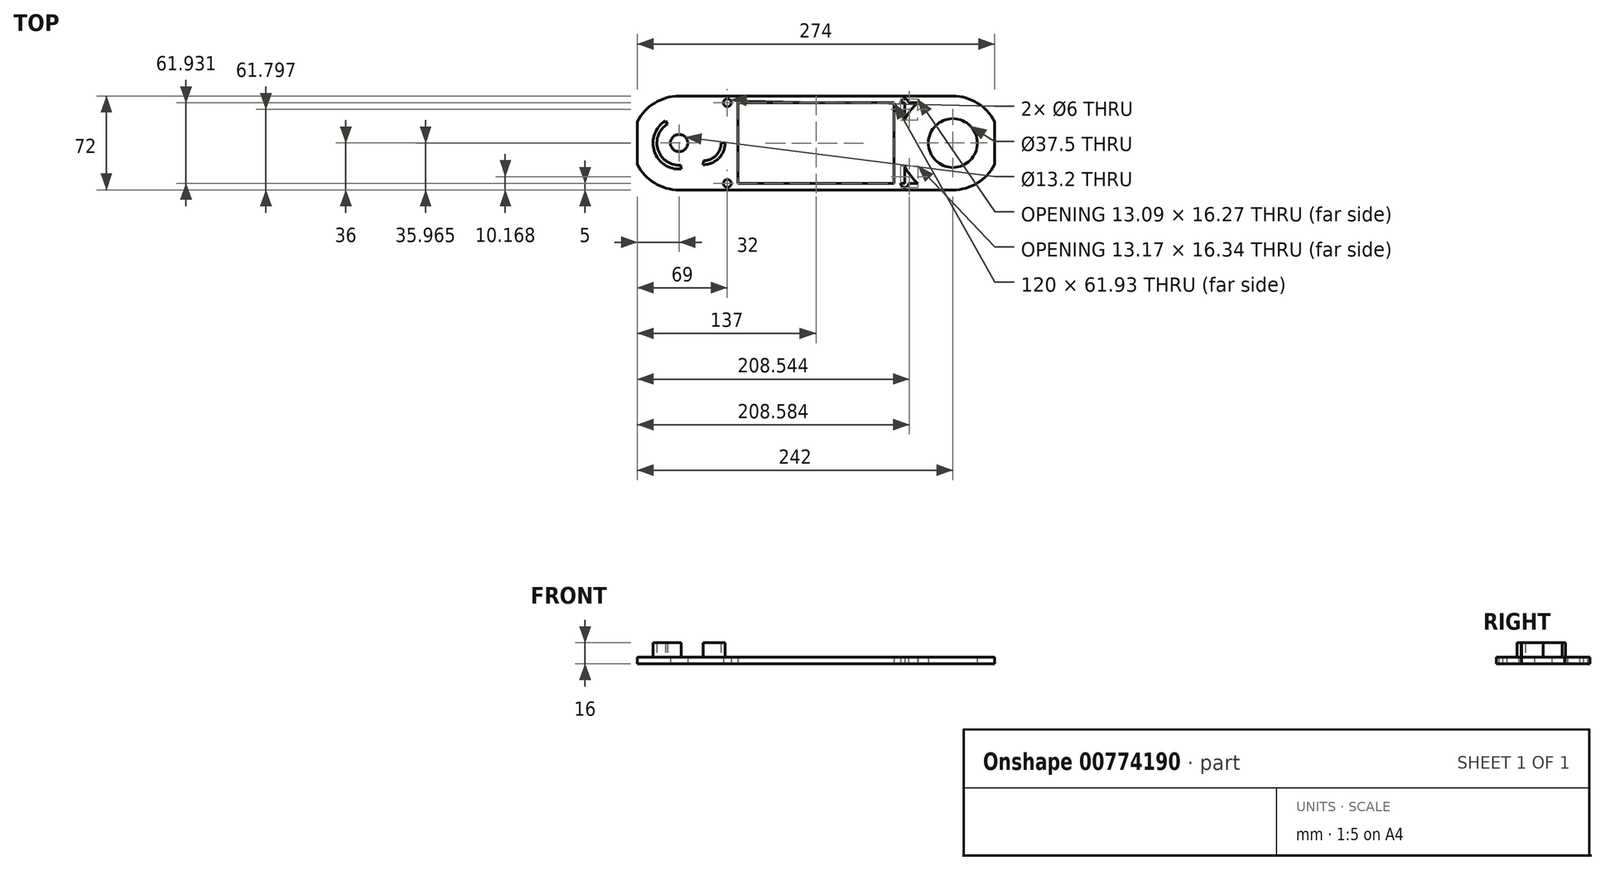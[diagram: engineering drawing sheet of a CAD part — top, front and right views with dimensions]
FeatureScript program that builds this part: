
annotation { "Feature Type Name" : "Feature", "Feature Type Description" : "" }
export const myFeature = defineFeature(function(context is Context, id is Id, definition is map)
    precondition{}
    {
        {
            var Q0;
            Q0=qCreatedBy(makeId("Top.planeOp"),FACE);
            var sketch = newSketch(context, id + "F0", { "sketchPlane" : qUnion([Q0])});
            skCircle(sketch, "E0", {"center": v(0, 0) * mm, "radius": 36 * mm});
            skCircle(sketch, "E1", {"center": v(210, 0) * mm, "radius": 36 * mm});
            skLineSegment(sketch, "E2", {"start": v(0, 36) * mm, "end": v(210, 36) * mm});
            skLineSegment(sketch, "E3", {"start": v(210, -36) * mm, "end": v(0, -36) * mm});
            skCircle(sketch, "E4", {"center": v(0, 0) * mm, "radius": 6.6 * mm});
            skCircle(sketch, "E5", {"center": v(0, 0) * mm, "radius": 10 * mm});
            skCircle(sketch, "E6", {"center": v(0, 0) * mm, "radius": 30 * mm});
            skCircle(sketch, "E7", {"center": v(210, 0) * mm, "radius": 30 * mm});
            skCircle(sketch, "E8", {"center": v(210, 0) * mm, "radius": 18.75 * mm});
            skCircle(sketch, "E9", {"center": v(210, 0) * mm, "radius": 21.5 * mm});
            skLineSegment(sketch, "E10", {"start": v(18.42, 30.93) * mm, "end": v(191.58, 30.93) * mm});
            skLineSegment(sketch, "E11", {"start": v(18.3, -31) * mm, "end": v(191.7, -31) * mm});
            skLineSegment(sketch, "E12", {"start": v(165, 30.93) * mm, "end": v(165, -31) * mm});
            skLineSegment(sketch, "E13", {"start": v(45, 30.93) * mm, "end": v(45, -31) * mm});
            skCircle(sketch, "E14", {"center": v(210, 0) * mm, "radius": 41 * mm});
            skCircle(sketch, "E15", {"center": v(0, 0) * mm, "radius": 41 * mm});
            skLineSegment(sketch, "E16.bottom", {"start": v(37, 30.93) * mm, "end": v(173, 30.93) * mm});
            skLineSegment(sketch, "E16.top", {"start": v(37, -31) * mm, "end": v(173, -31) * mm});
            skLineSegment(sketch, "E16.left", {"start": v(37, 30.93) * mm, "end": v(37, -31) * mm});
            skLineSegment(sketch, "E16.right", {"start": v(173, 30.93) * mm, "end": v(173, -31) * mm});
            skCircle(sketch, "E17", {"center": v(37, 30.93) * mm, "radius": 3 * mm});
            skCircle(sketch, "E18", {"center": v(37, -31) * mm, "radius": 3 * mm});
            skCircle(sketch, "E19", {"center": v(173, 30.93) * mm, "radius": 3 * mm});
            skCircle(sketch, "E20", {"center": v(173, -31) * mm, "radius": 3 * mm});
            skLineSegment(sketch, "E21", {"start": v(-32, -16.5) * mm, "end": v(-32, 16.5) * mm});
            skLineSegment(sketch, "E22", {"start": v(242, -16.5) * mm, "end": v(242, 16.5) * mm});
            skSolve(sketch);
        }
        {
            var Q0;
            {var subQ0=sQuery(id+"F0.wireOp",EDGE,"E16.left");var subQ1=sQuery(id+"F0.wireOp",EDGE,"E15");var subQ2=makeQuery(id+"F0.imprint","INTERSECT",VERTEX,{"disambiguationData":[OD(0.0)],"derivedFrom":[subQ1,subQ0]});Q0=makeQuery(id+"F0.imprint","IMPRINT",FACE,{"disambiguationData":[TD([[makeQuery(id+"F0.imprint","IMPRINT",EDGE,{"disambiguationData":[TD([[subQ2,1.0]])],"derivedFrom":subQ1}),1.0]])]});}
            var Q1;
            Q1=makeQuery(id+"F0.imprint","IMPRINT",FACE,{"disambiguationData":[TD([[makeQuery(id+"F0.imprint","IMPRINT",EDGE,{"derivedFrom":sQuery(id+"F0.wireOp",EDGE,"E4")}),-1.0]])]});
            var Q2;
            {var subQ0=sQuery(id+"F0.wireOp",EDGE,"E2");var subQ1=sQuery(id+"F0.wireOp",EDGE,"E1");var subQ2=makeQuery(id+"F0.imprint","INTERSECT",VERTEX,{"derivedFrom":[subQ1,subQ0]});Q2=makeQuery(id+"F0.imprint","IMPRINT",FACE,{"disambiguationData":[TD([[makeQuery(id+"F0.imprint","IMPRINT",EDGE,{"disambiguationData":[TD([[subQ2,-1.0]])],"derivedFrom":subQ1}),-1.0]])]});}
            var Q3;
            Q3=makeQuery(id+"F0.imprint","IMPRINT",FACE,{"disambiguationData":[TD([[makeQuery(id+"F0.imprint","IMPRINT",EDGE,{"derivedFrom":sQuery(id+"F0.wireOp",EDGE,"E5")}),-1.0]])]});
            var Q4;
            Q4=makeQuery(id+"F0.imprint","IMPRINT",FACE,{"disambiguationData":[TD([[makeQuery(id+"F0.imprint","IMPRINT",EDGE,{"derivedFrom":sQuery(id+"F0.wireOp",EDGE,"E8")}),-1.0]])]});
            var Q5;
            {var subQ0=sQuery(id+"F0.wireOp",EDGE,"E3");var subQ1=sQuery(id+"F0.wireOp",EDGE,"E0");var subQ2=makeQuery(id+"F0.imprint","INTERSECT",VERTEX,{"derivedFrom":[subQ1,subQ0]});Q5=makeQuery(id+"F0.imprint","IMPRINT",FACE,{"disambiguationData":[TD([[makeQuery(id+"F0.imprint","IMPRINT",EDGE,{"disambiguationData":[TD([[subQ2,-1.0]])],"derivedFrom":subQ1}),-1.0]])]});}
            var Q6;
            Q6=makeQuery(id+"F0.imprint","IMPRINT",FACE,{"disambiguationData":[TD([[makeQuery(id+"F0.imprint","IMPRINT",EDGE,{"derivedFrom":sQuery(id+"F0.wireOp",EDGE,"E7")}),-1.0]])]});
            var Q7;
            Q7=makeQuery(id+"F0.imprint","IMPRINT",FACE,{"disambiguationData":[TD([[makeQuery(id+"F0.imprint","IMPRINT",EDGE,{"derivedFrom":sQuery(id+"F0.wireOp",EDGE,"E7")}),1.0]])]});
            var Q8;
            Q8=makeQuery(id+"F0.imprint","IMPRINT",FACE,{"disambiguationData":[TD([[makeQuery(id+"F0.imprint","IMPRINT",EDGE,{"derivedFrom":sQuery(id+"F0.wireOp",EDGE,"E6")}),-1.0]])]});
            var Q9;
            {var subQ1=sQuery(id+"F0.wireOp",EDGE,"E10");var subQ5=sQuery(id+"F0.wireOp",EDGE,"E0");var subQ6=makeQuery(id+"F0.imprint","INTERSECT",VERTEX,{"derivedFrom":[subQ5,subQ1]});Q9=makeQuery(id+"F0.imprint","IMPRINT",FACE,{"disambiguationData":[TD([[makeQuery(id+"F0.imprint","IMPRINT",EDGE,{"disambiguationData":[TD([[subQ6,1.0]])],"derivedFrom":subQ5}),-1.0]])]});}
            var Q10;
            {var subQ1=sQuery(id+"F0.wireOp",EDGE,"E12");Q10=makeQuery(id+"F0.imprint","IMPRINT",FACE,{"disambiguationData":[TD([[makeQuery(id+"F0.imprint","IMPRINT",EDGE,{"derivedFrom":subQ1}),1.0]])]});}
            var Q11;
            {var subQ1=sQuery(id+"F0.wireOp",EDGE,"E1");var subQ5=sQuery(id+"F0.wireOp",EDGE,"E10");var subQ9=makeQuery(id+"F0.imprint","INTERSECT",VERTEX,{"derivedFrom":[subQ1,subQ5]});Q11=makeQuery(id+"F0.imprint","IMPRINT",FACE,{"disambiguationData":[TD([[makeQuery(id+"F0.imprint","IMPRINT",EDGE,{"disambiguationData":[TD([[subQ9,-1.0]])],"derivedFrom":subQ1}),-1.0]])]});}
            var Q12;
            {var subQ0=sQuery(id+"F0.wireOp",EDGE,"E19");var subQ1=sQuery(id+"F0.wireOp",EDGE,"E10");var subQ2=makeQuery(id+"F0.imprint","INTERSECT",VERTEX,{"derivedFrom":[subQ1,subQ0]});Q12=makeQuery(id+"F0.imprint","IMPRINT",FACE,{"disambiguationData":[TD([[makeQuery(id+"F0.imprint","IMPRINT",EDGE,{"disambiguationData":[TD([[subQ2,-1.0]])],"derivedFrom":subQ1}),-1.0]])]});}
            var Q13;
            {var subQ1=sQuery(id+"F0.wireOp",EDGE,"E13");Q13=makeQuery(id+"F0.imprint","IMPRINT",FACE,{"disambiguationData":[TD([[makeQuery(id+"F0.imprint","IMPRINT",EDGE,{"derivedFrom":subQ1}),-1.0]])]});}
            var Q14;
            {var subQ0=sQuery(id+"F0.wireOp",EDGE,"E2");var subQ1=sQuery(id+"F0.wireOp",EDGE,"E0");var subQ2=makeQuery(id+"F0.imprint","INTERSECT",VERTEX,{"derivedFrom":[subQ1,subQ0]});Q14=makeQuery(id+"F0.imprint","IMPRINT",FACE,{"disambiguationData":[TD([[makeQuery(id+"F0.imprint","IMPRINT",EDGE,{"disambiguationData":[TD([[subQ2,1.0]])],"derivedFrom":subQ1}),-1.0]])]});}
            var Q15;
            {var subQ0=sQuery(id+"F0.wireOp",EDGE,"E20");var subQ1=sQuery(id+"F0.wireOp",EDGE,"E11");var subQ2=makeQuery(id+"F0.imprint","INTERSECT",VERTEX,{"derivedFrom":[subQ1,subQ0]});Q15=makeQuery(id+"F0.imprint","IMPRINT",FACE,{"disambiguationData":[TD([[makeQuery(id+"F0.imprint","IMPRINT",EDGE,{"disambiguationData":[TD([[subQ2,-1.0]])],"derivedFrom":subQ1}),1.0]])]});}
            var Q16;
            {var subQ0=sQuery(id+"F0.wireOp",EDGE,"E15");var subQ1=sQuery(id+"F0.wireOp",EDGE,"E10");var subQ2=makeQuery(id+"F0.imprint","INTERSECT",VERTEX,{"derivedFrom":[subQ1,subQ0]});Q16=makeQuery(id+"F0.imprint","IMPRINT",FACE,{"disambiguationData":[TD([[makeQuery(id+"F0.imprint","IMPRINT",EDGE,{"disambiguationData":[TD([[subQ2,-1.0]])],"derivedFrom":subQ1}),-1.0]])]});}
            var Q17;
            {var subQ0=sQuery(id+"F0.wireOp",EDGE,"E14");var subQ1=sQuery(id+"F0.wireOp",EDGE,"E3");var subQ2=makeQuery(id+"F0.imprint","INTERSECT",VERTEX,{"derivedFrom":[subQ1,subQ0]});Q17=makeQuery(id+"F0.imprint","IMPRINT",FACE,{"disambiguationData":[TD([[makeQuery(id+"F0.imprint","IMPRINT",EDGE,{"disambiguationData":[TD([[subQ2,-1.0]])],"derivedFrom":subQ1}),-1.0]])]});}
            var Q18;
            {var subQ0=sQuery(id+"F0.wireOp",EDGE,"E15");var subQ6=sQuery(id+"F0.wireOp",EDGE,"E2");var subQ11=makeQuery(id+"F0.imprint","INTERSECT",VERTEX,{"derivedFrom":[subQ6,subQ0]});Q18=makeQuery(id+"F0.imprint","IMPRINT",FACE,{"disambiguationData":[TD([[makeQuery(id+"F0.imprint","IMPRINT",EDGE,{"disambiguationData":[TD([[subQ11,-1.0]])],"derivedFrom":subQ6}),-1.0]])]});}
            var Q19;
            {var subQ0=sQuery(id+"F0.wireOp",EDGE,"E16.right");var subQ1=sQuery(id+"F0.wireOp",EDGE,"E14");var subQ2=makeQuery(id+"F0.imprint","INTERSECT",VERTEX,{"disambiguationData":[OD(0.0)],"derivedFrom":[subQ1,subQ0]});Q19=makeQuery(id+"F0.imprint","IMPRINT",FACE,{"disambiguationData":[TD([[makeQuery(id+"F0.imprint","IMPRINT",EDGE,{"disambiguationData":[TD([[subQ2,-1.0]])],"derivedFrom":subQ1}),1.0]])]});}
            var Q20;
            {var subQ0=sQuery(id+"F0.wireOp",EDGE,"E15");var subQ1=sQuery(id+"F0.wireOp",EDGE,"E11");var subQ2=makeQuery(id+"F0.imprint","INTERSECT",VERTEX,{"derivedFrom":[subQ1,subQ0]});Q20=makeQuery(id+"F0.imprint","IMPRINT",FACE,{"disambiguationData":[TD([[makeQuery(id+"F0.imprint","IMPRINT",EDGE,{"disambiguationData":[TD([[subQ2,-1.0]])],"derivedFrom":subQ1}),1.0]])]});}
            var Q21;
            {var subQ0=sQuery(id+"F0.wireOp",EDGE,"E3");var subQ1=sQuery(id+"F0.wireOp",EDGE,"E1");var subQ2=makeQuery(id+"F0.imprint","INTERSECT",VERTEX,{"derivedFrom":[subQ1,subQ0]});Q21=makeQuery(id+"F0.imprint","IMPRINT",FACE,{"disambiguationData":[TD([[makeQuery(id+"F0.imprint","IMPRINT",EDGE,{"disambiguationData":[TD([[subQ2,1.0]])],"derivedFrom":subQ1}),-1.0]])]});}
            extrude(context, id + "F1", {"entities" : qUnion([Q0, Q1, Q2, Q3, Q4, Q5, Q6, Q7, Q8, Q9, Q10, Q11, Q12, Q13, Q14, Q15, Q16, Q17, Q18, Q19, Q20, Q21]), "depth" : 5 * mm, "offsetDistance" : 25 * mm});
        }
        {
            var Q0;
            Q0=makeQuery(id+"F1.opExtrude","CAP_FACE",FACE,{"disambiguationData":[OSD([sQuery(id+"F0.wireOp",EDGE,"E0"),sQuery(id+"F0.wireOp",EDGE,"E1"),sQuery(id+"F0.wireOp",EDGE,"E2"),sQuery(id+"F0.wireOp",EDGE,"E3"),sQuery(id+"F0.wireOp",EDGE,"E4"),sQuery(id+"F0.wireOp",EDGE,"E8"),sQuery(id+"F0.wireOp",EDGE,"E12"),sQuery(id+"F0.wireOp",EDGE,"E13"),sQuery(id+"F0.wireOp",EDGE,"E16.bottom"),sQuery(id+"F0.wireOp",EDGE,"E16.top"),sQuery(id+"F0.wireOp",EDGE,"E17"),sQuery(id+"F0.wireOp",EDGE,"E18"),sQuery(id+"F0.wireOp",EDGE,"E19"),sQuery(id+"F0.wireOp",EDGE,"E20"),sQuery(id+"F0.wireOp",EDGE,"E21"),sQuery(id+"F0.wireOp",EDGE,"E22")])],"isStart":false});
            var sketch = newSketch(context, id + "F2", { "sketchPlane" : qUnion([Q0])});
            skCircle(sketch, "E23", {"center": v(0, 0) * mm, "radius": 2.1 * mm});
            skArc(sketch, "E24", {"start": v(-5.63, 16.04) * mm, "mid": v(-16.62, -3.54) * mm, "end": v(1.4, -16.94) * mm});
            skArc(sketch, "E25.0", {"start": v(-6.63, 18.87) * mm, "mid": v(-19.55, -4.17) * mm, "end": v(1.65, -19.93) * mm});
            skLineSegment(sketch, "E26", {"start": v(-6.63, 18.87) * mm, "end": v(-5.63, 16.04) * mm});
            skLineSegment(sketch, "E27", {"start": v(1.65, -19.93) * mm, "end": v(1.4, -16.94) * mm});
            skArc(sketch, "E28", {"start": v(18.63, -13.6) * mm, "mid": v(28.25, -9.62) * mm, "end": v(32.23, 0) * mm});
            skArc(sketch, "E29.0", {"start": v(18.63, -16.6) * mm, "mid": v(30.37, -11.74) * mm, "end": v(35.23, 0) * mm});
            skLineSegment(sketch, "E30", {"start": v(18.63, -13.6) * mm, "end": v(18.63, -16.6) * mm});
            skLineSegment(sketch, "E31", {"start": v(32.23, 0) * mm, "end": v(35.23, 0) * mm});
            skLineSegment(sketch, "E32", {"start": v(-6.63, 18.87) * mm, "end": v(-10.56, 16.98) * mm});
            skLineSegment(sketch, "E33", {"start": v(-10.56, 16.98) * mm, "end": v(-8.85, 14.51) * mm});
            skSolve(sketch);
        }
        {
            var Q0;
            Q0=makeQuery(id+"F2.imprint","IMPRINT",FACE,{"disambiguationData":[TD([[makeQuery(id+"F2.imprint","IMPRINT",EDGE,{"derivedFrom":sQuery(id+"F2.wireOp",EDGE,"E28")}),-1.0]])]});
            var Q1;
            {var subQ0=sQuery(id+"F2.wireOp",EDGE,"E27");Q1=makeQuery(id+"F2.imprint","IMPRINT",FACE,{"disambiguationData":[TD([[makeQuery(id+"F2.imprint","IMPRINT",EDGE,{"derivedFrom":subQ0}),1.0]])]});}
            extrude(context, id + "F3", {"entities" : qUnion([Q0, Q1]), "operationType" : NewBodyOperationType.ADD, "depth" : 11 * mm, "offsetDistance" : 25 * mm});
        }
    });
